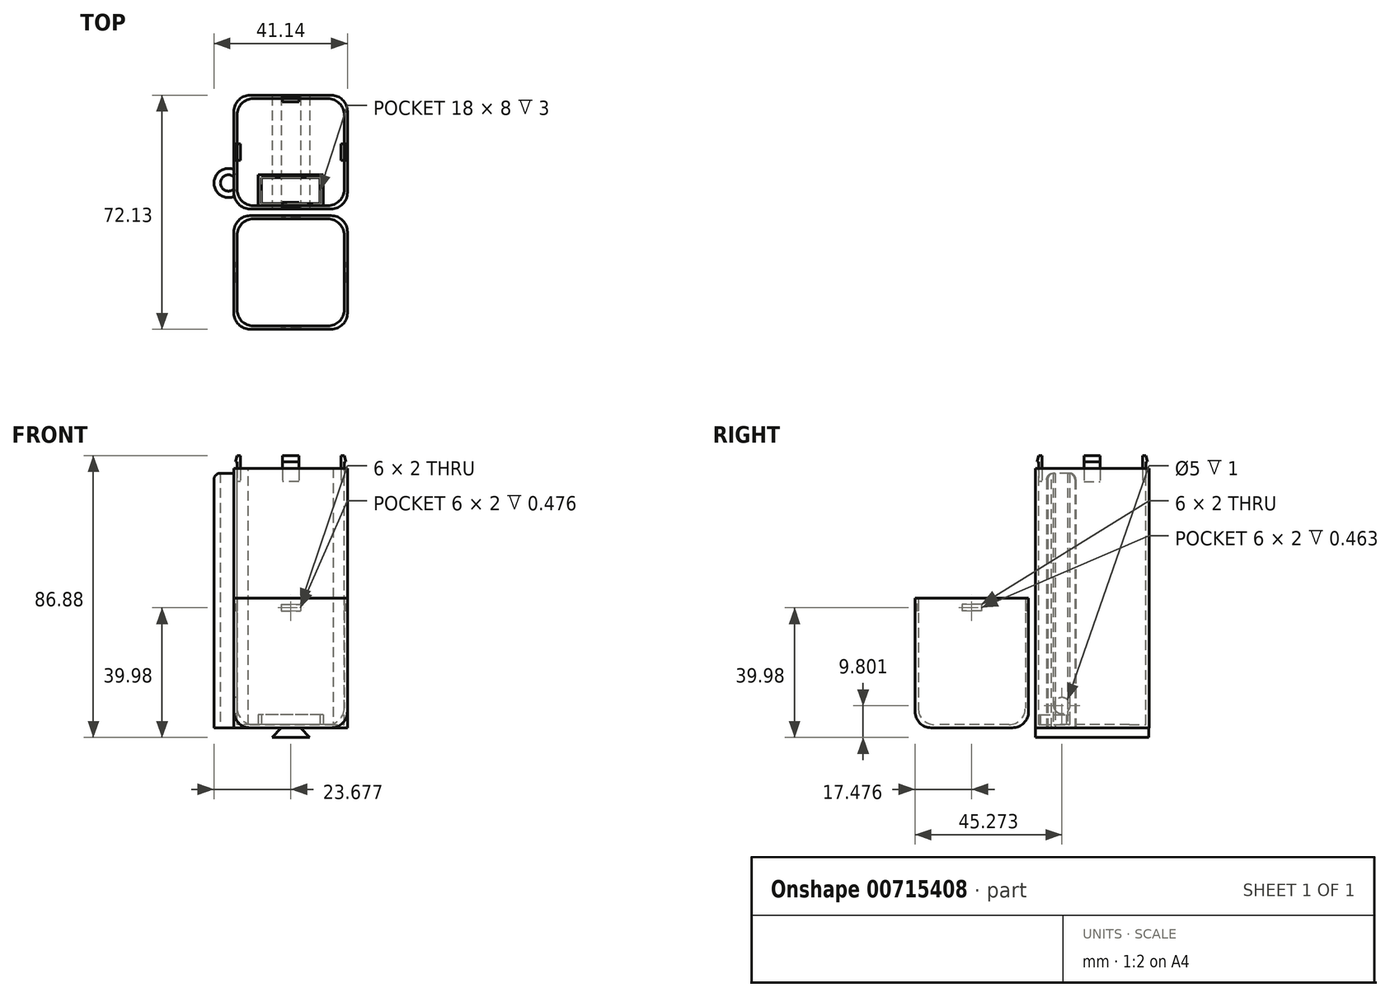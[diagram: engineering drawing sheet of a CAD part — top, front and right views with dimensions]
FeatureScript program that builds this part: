
annotation { "Feature Type Name" : "Feature", "Feature Type Description" : "" }
export const myFeature = defineFeature(function(context is Context, id is Id, definition is map)
    precondition{}
    {
        {
            var Q0;
            Q0=qCreatedBy(makeId("Top.planeOp"),FACE);
            var sketch = newSketch(context, id + "F0", { "sketchPlane" : qUnion([Q0])});
            skLineSegment(sketch, "E0.bottom", {"start": v(0, 0) * mm, "end": v(35, 0) * mm});
            skLineSegment(sketch, "E0.top", {"start": v(0, -35) * mm, "end": v(35, -35) * mm});
            skLineSegment(sketch, "E0.left", {"start": v(0, 0) * mm, "end": v(0, -35) * mm});
            skLineSegment(sketch, "E0.right", {"start": v(35, 0) * mm, "end": v(35, -35) * mm});
            skLineSegment(sketch, "E1.bottom", {"start": v(2.41, -2.74) * mm, "end": v(32.41, -2.74) * mm, "construction": true});
            skLineSegment(sketch, "E1.top", {"start": v(2.41, -32.74) * mm, "end": v(32.41, -32.74) * mm, "construction": true});
            skLineSegment(sketch, "E1.left", {"start": v(2.41, -2.74) * mm, "end": v(2.41, -32.74) * mm, "construction": true});
            skLineSegment(sketch, "E1.right", {"start": v(32.41, -2.74) * mm, "end": v(32.41, -32.74) * mm, "construction": true});
            skLineSegment(sketch, "E2.0", {"start": v(1, -1) * mm, "end": v(34, -1) * mm});
            skLineSegment(sketch, "E2.1", {"start": v(1, -1) * mm, "end": v(1, -34) * mm});
            skLineSegment(sketch, "E2.2", {"start": v(1, -34) * mm, "end": v(34, -34) * mm});
            skLineSegment(sketch, "E2.3", {"start": v(34, -1) * mm, "end": v(34, -34) * mm});
            skLineSegment(sketch, "E3", {"start": v(17.5, -35) * mm, "end": v(17.5, 0) * mm, "construction": true});
            skLineSegment(sketch, "E4", {"start": v(0, -17.5) * mm, "end": v(35, -17.5) * mm});
            skCircle(sketch, "E5", {"center": v(17.5, -17.5) * mm, "radius": 16.5 * mm});
            skSolve(sketch);
        }
        {
            var Q0;
            Q0 = qSketchRegion(id + "F0", true);
            extrude(context, id + "F1", {"entities" : qUnion([Q0]), "depth" : 40 * mm, "offsetDistance" : 25 * mm});
        }
        {
            var Q0;
            Q0 = qSketchRegion(id + "F0", true);
            extrude(context, id + "F2", {"entities" : qUnion([Q0]), "depth" : 80 * mm, "offsetDistance" : 25 * mm});
        }
        {
            var Q0;
            Q0=makeQuery(id+"F2.opExtrude","SWEPT_BODY",BODY,{"disambiguationData":[OSD([sQuery(id+"F0.wireOp",EDGE,"E0.bottom"),sQuery(id+"F0.wireOp",EDGE,"E0.top"),sQuery(id+"F0.wireOp",EDGE,"E0.left"),sQuery(id+"F0.wireOp",EDGE,"E0.right"),sQuery(id+"F0.wireOp",EDGE,"E2.0"),sQuery(id+"F0.wireOp",EDGE,"E2.1"),sQuery(id+"F0.wireOp",EDGE,"E2.2"),sQuery(id+"F0.wireOp",EDGE,"E2.3")])]});
            transform(context, id + "F3", {"entities" : qUnion([Q0]), "transformType" : TransformType.TRANSLATION_3D, "dx" : 0 * mm, "dy" : 0 * mm, "dz" : 45 * mm, "makeCopy" : false});
        }
        {
            var Q0;
            Q0=qCreatedBy(makeId("Top.planeOp"),FACE);
            var sketch = newSketch(context, id + "F4", { "sketchPlane" : qUnion([Q0])});
            skLineSegment(sketch, "E6.bottom", {"start": v(20.54, -0.52) * mm, "end": v(14.54, -0.52) * mm});
            skLineSegment(sketch, "E6.top", {"start": v(20.54, -34.52) * mm, "end": v(14.54, -34.52) * mm});
            skLineSegment(sketch, "E6.left", {"start": v(20.54, -0.52) * mm, "end": v(20.54, -34.52) * mm});
            skLineSegment(sketch, "E6.right", {"start": v(14.54, -0.52) * mm, "end": v(14.54, -34.52) * mm});
            skPoint(sketch, "E6.middle", {"position": v(17.54, -17.52) * mm});
            skPoint(sketch, "E6.middle.positionSnap0", {"position": v(14.24, -17.52) * mm});
            skLineSegment(sketch, "E7.bottom", {"start": v(34.54, -20.52) * mm, "end": v(0.54, -20.52) * mm});
            skLineSegment(sketch, "E7.top", {"start": v(34.54, -14.52) * mm, "end": v(0.54, -14.52) * mm});
            skLineSegment(sketch, "E7.left", {"start": v(34.54, -20.52) * mm, "end": v(34.54, -14.52) * mm});
            skLineSegment(sketch, "E7.right", {"start": v(0.54, -20.52) * mm, "end": v(0.54, -14.52) * mm});
            skSolve(sketch);
        }
        {
            var Q0;
            Q0 = qSketchRegion(id + "F4", true);
            extrude(context, id + "F5", {"entities" : qUnion([Q0]), "operationType" : NewBodyOperationType.REMOVE, "depth" : 38 * mm, "offsetDistance" : 25 * mm, "hasSecondDirection" : true, "secondDirectionOppositeDirection" : false, "secondDirectionDepth" : 36 * mm});
        }
        {
            var Q0;
            Q0=qCreatedBy(makeId("Right.planeOp"),FACE);
            var sketch = newSketch(context, id + "F6", { "sketchPlane" : qUnion([Q0])});
            skLineSegment(sketch, "E8.bottom", {"start": v(-33, 41.1) * mm, "end": v(-34, 41.1) * mm});
            skLineSegment(sketch, "E8.top", {"start": v(-33, 49.1) * mm, "end": v(-34, 49.1) * mm});
            skLineSegment(sketch, "E8.left", {"start": v(-33, 41.1) * mm, "end": v(-33, 49.1) * mm});
            skLineSegment(sketch, "E8.right", {"start": v(-34, 41.1) * mm, "end": v(-34, 49.1) * mm});
            skPoint(sketch, "E8.middle", {"position": v(-33.5, 45.1) * mm});
            skLineSegment(sketch, "E9", {"start": v(-34, 41.1) * mm, "end": v(-34.5, 43) * mm});
            skLineSegment(sketch, "E10", {"start": v(-34.5, 43) * mm, "end": v(-34, 43) * mm});
            skSolve(sketch);
        }
        {
            var Q0;
            {var subQ1=sQuery(id+"F6.wireOp",EDGE,"E8.bottom");Q0=makeQuery(id+"F6.imprint","IMPRINT",FACE,{"disambiguationData":[TD([[makeQuery(id+"F6.imprint","IMPRINT",EDGE,{"derivedFrom":subQ1}),-1.0]])]});}
            var Q1;
            {var subQ0=sQuery(id+"F6.wireOp",EDGE,"E9");Q1=makeQuery(id+"F6.imprint","IMPRINT",FACE,{"disambiguationData":[TD([[makeQuery(id+"F6.imprint","IMPRINT",EDGE,{"derivedFrom":subQ0}),-1.0]])]});}
            extrude(context, id + "F7", {"entities" : qUnion([Q0, Q1]), "depth" : 20 * mm, "offsetDistance" : 25 * mm, "hasSecondDirection" : true, "secondDirectionOppositeDirection" : false, "secondDirectionDepth" : 15 * mm});
        }
        {
            var Q0;
            Q0=makeQuery(id+"F7.opExtrude","SWEPT_BODY",BODY,{"disambiguationData":[OSD([sQuery(id+"F6.wireOp",EDGE,"E8.bottom"),sQuery(id+"F6.wireOp",EDGE,"E8.top"),sQuery(id+"F6.wireOp",EDGE,"E8.left"),sQuery(id+"F6.wireOp",EDGE,"E8.right"),sQuery(id+"F6.wireOp",EDGE,"E9"),sQuery(id+"F6.wireOp",EDGE,"E10")])]});
            var Q1;
            Q1=sQuery(id+"F0.wireOp",EDGE,"E5");
            circularPattern(context, id + "F8", {"operationType" : NewBodyOperationType.ADD, "entities" : qUnion([Q0]), "axis" : qUnion([Q1]), "angle" : 360 * degree, "instanceCount" : 4, "equalSpace" : true});
        }
        {
            var Q0;
            Q0=qCreatedBy(makeId("Top.planeOp"),FACE);
            var sketch = newSketch(context, id + "F9", { "sketchPlane" : qUnion([Q0])});
            skLineSegment(sketch, "E11.bottom", {"start": v(0, 37.13) * mm, "end": v(35, 37.13) * mm});
            skLineSegment(sketch, "E11.top", {"start": v(0, 2.13) * mm, "end": v(35, 2.13) * mm});
            skLineSegment(sketch, "E11.left", {"start": v(0, 37.13) * mm, "end": v(0, 2.13) * mm});
            skLineSegment(sketch, "E11.right", {"start": v(35, 37.13) * mm, "end": v(35, 2.13) * mm});
            skLineSegment(sketch, "E12", {"start": v(17.5, 37.13) * mm, "end": v(17.5, 2.13) * mm, "construction": true});
            skLineSegment(sketch, "E13", {"start": v(17.5, 2.13) * mm, "end": v(0, 19.63) * mm, "construction": true});
            skLineSegment(sketch, "E14", {"start": v(0, 19.63) * mm, "end": v(35, 19.63) * mm, "construction": true});
            skLineSegment(sketch, "E15", {"start": v(35, 19.63) * mm, "end": v(17.5, 37.13) * mm, "construction": true});
            skLineSegment(sketch, "E16.bottom", {"start": v(27.5, 2.67) * mm, "end": v(7.5, 2.67) * mm});
            skLineSegment(sketch, "E16.top", {"start": v(27.5, 12.67) * mm, "end": v(7.5, 12.67) * mm});
            skLineSegment(sketch, "E16.left", {"start": v(27.5, 2.67) * mm, "end": v(27.5, 12.67) * mm});
            skLineSegment(sketch, "E16.right", {"start": v(7.5, 2.67) * mm, "end": v(7.5, 12.67) * mm});
            skPoint(sketch, "E16.middle", {"position": v(17.5, 7.67) * mm});
            skLineSegment(sketch, "E17.0", {"start": v(26.5, 11.67) * mm, "end": v(8.5, 11.67) * mm});
            skLineSegment(sketch, "E17.1", {"start": v(26.5, 3.67) * mm, "end": v(26.5, 11.67) * mm});
            skLineSegment(sketch, "E17.2", {"start": v(26.5, 3.67) * mm, "end": v(8.5, 3.67) * mm});
            skLineSegment(sketch, "E17.3", {"start": v(8.5, 3.67) * mm, "end": v(8.5, 11.67) * mm});
            skSolve(sketch);
        }
        {
            var Q0;
            Q0=makeQuery(id+"F2.opExtrude","SWEPT_BODY",BODY,{"disambiguationData":[OSD([sQuery(id+"F0.wireOp",EDGE,"E0.bottom"),sQuery(id+"F0.wireOp",EDGE,"E0.top"),sQuery(id+"F0.wireOp",EDGE,"E0.left"),sQuery(id+"F0.wireOp",EDGE,"E0.right"),sQuery(id+"F0.wireOp",EDGE,"E2.0"),sQuery(id+"F0.wireOp",EDGE,"E2.1"),sQuery(id+"F0.wireOp",EDGE,"E2.2"),sQuery(id+"F0.wireOp",EDGE,"E2.3")])]});
            var Q1;
            Q1=makeQuery(id+"F8.opPattern","COPY",BODY,{"derivedFrom":makeQuery(id+"F7.opExtrude","SWEPT_BODY",BODY,{"disambiguationData":[OSD([sQuery(id+"F6.wireOp",EDGE,"E8.bottom"),sQuery(id+"F6.wireOp",EDGE,"E8.top"),sQuery(id+"F6.wireOp",EDGE,"E8.left"),sQuery(id+"F6.wireOp",EDGE,"E8.right"),sQuery(id+"F6.wireOp",EDGE,"E9"),sQuery(id+"F6.wireOp",EDGE,"E10")])]}),"instanceName":"1"});
            var Q2;
            Q2=makeQuery(id+"F8.opPattern","COPY",BODY,{"derivedFrom":makeQuery(id+"F7.opExtrude","SWEPT_BODY",BODY,{"disambiguationData":[OSD([sQuery(id+"F6.wireOp",EDGE,"E8.bottom"),sQuery(id+"F6.wireOp",EDGE,"E8.top"),sQuery(id+"F6.wireOp",EDGE,"E8.left"),sQuery(id+"F6.wireOp",EDGE,"E8.right"),sQuery(id+"F6.wireOp",EDGE,"E9"),sQuery(id+"F6.wireOp",EDGE,"E10")])]}),"instanceName":"3"});
            var Q3;
            Q3=makeQuery(id+"F7.opExtrude","SWEPT_BODY",BODY,{"disambiguationData":[OSD([sQuery(id+"F6.wireOp",EDGE,"E8.bottom"),sQuery(id+"F6.wireOp",EDGE,"E8.top"),sQuery(id+"F6.wireOp",EDGE,"E8.left"),sQuery(id+"F6.wireOp",EDGE,"E8.right"),sQuery(id+"F6.wireOp",EDGE,"E9"),sQuery(id+"F6.wireOp",EDGE,"E10")])]});
            var Q4;
            Q4=makeQuery(id+"F8.opPattern","COPY",BODY,{"derivedFrom":makeQuery(id+"F7.opExtrude","SWEPT_BODY",BODY,{"disambiguationData":[OSD([sQuery(id+"F6.wireOp",EDGE,"E8.bottom"),sQuery(id+"F6.wireOp",EDGE,"E8.top"),sQuery(id+"F6.wireOp",EDGE,"E8.left"),sQuery(id+"F6.wireOp",EDGE,"E8.right"),sQuery(id+"F6.wireOp",EDGE,"E9"),sQuery(id+"F6.wireOp",EDGE,"E10")])]}),"instanceName":"2"});
            var Q5;
            Q5=makeQuery(id+"F2.opExtrude","CAP_EDGE",EDGE,{"disambiguationData":[OSD([sQuery(id+"F0.wireOp",EDGE,"E0.bottom")])],"isStart":true});
            transform(context, id + "F10", {"entities" : qUnion([Q0, Q1, Q2, Q3, Q4]), "transformType" : TransformType.ROTATION, "transformAxis" : qUnion([Q5]), "angle" : 180 * degree, "makeCopy" : false});
        }
        {
            var Q0;
            Q0=makeQuery(id+"F2.opExtrude","SWEPT_BODY",BODY,{"disambiguationData":[OSD([sQuery(id+"F0.wireOp",EDGE,"E0.bottom"),sQuery(id+"F0.wireOp",EDGE,"E0.top"),sQuery(id+"F0.wireOp",EDGE,"E0.left"),sQuery(id+"F0.wireOp",EDGE,"E0.right"),sQuery(id+"F0.wireOp",EDGE,"E2.0"),sQuery(id+"F0.wireOp",EDGE,"E2.1"),sQuery(id+"F0.wireOp",EDGE,"E2.2"),sQuery(id+"F0.wireOp",EDGE,"E2.3")])]});
            var Q1;
            Q1=makeQuery(id+"F7.opExtrude","SWEPT_BODY",BODY,{"disambiguationData":[OSD([sQuery(id+"F6.wireOp",EDGE,"E8.bottom"),sQuery(id+"F6.wireOp",EDGE,"E8.top"),sQuery(id+"F6.wireOp",EDGE,"E8.left"),sQuery(id+"F6.wireOp",EDGE,"E8.right"),sQuery(id+"F6.wireOp",EDGE,"E9"),sQuery(id+"F6.wireOp",EDGE,"E10")])]});
            var Q2;
            Q2=makeQuery(id+"F8.opPattern","COPY",BODY,{"derivedFrom":makeQuery(id+"F7.opExtrude","SWEPT_BODY",BODY,{"disambiguationData":[OSD([sQuery(id+"F6.wireOp",EDGE,"E8.bottom"),sQuery(id+"F6.wireOp",EDGE,"E8.top"),sQuery(id+"F6.wireOp",EDGE,"E8.left"),sQuery(id+"F6.wireOp",EDGE,"E8.right"),sQuery(id+"F6.wireOp",EDGE,"E9"),sQuery(id+"F6.wireOp",EDGE,"E10")])]}),"instanceName":"1"});
            var Q3;
            Q3=makeQuery(id+"F8.opPattern","COPY",BODY,{"derivedFrom":makeQuery(id+"F7.opExtrude","SWEPT_BODY",BODY,{"disambiguationData":[OSD([sQuery(id+"F6.wireOp",EDGE,"E8.bottom"),sQuery(id+"F6.wireOp",EDGE,"E8.top"),sQuery(id+"F6.wireOp",EDGE,"E8.left"),sQuery(id+"F6.wireOp",EDGE,"E8.right"),sQuery(id+"F6.wireOp",EDGE,"E9"),sQuery(id+"F6.wireOp",EDGE,"E10")])]}),"instanceName":"2"});
            var Q4;
            Q4=makeQuery(id+"F8.opPattern","COPY",BODY,{"derivedFrom":makeQuery(id+"F7.opExtrude","SWEPT_BODY",BODY,{"disambiguationData":[OSD([sQuery(id+"F6.wireOp",EDGE,"E8.bottom"),sQuery(id+"F6.wireOp",EDGE,"E8.top"),sQuery(id+"F6.wireOp",EDGE,"E8.left"),sQuery(id+"F6.wireOp",EDGE,"E8.right"),sQuery(id+"F6.wireOp",EDGE,"E9"),sQuery(id+"F6.wireOp",EDGE,"E10")])]}),"instanceName":"3"});
            transform(context, id + "F11", {"entities" : qUnion([Q0, Q1, Q2, Q3, Q4]), "transformType" : TransformType.TRANSLATION_3D, "dx" : 0 * mm, "dy" : 2.1 * mm, "dz" : 35 * mm, "makeCopy" : false});
        }
        {
            var Q0;
            {var subQ7=sQuery(id+"F0.wireOp",EDGE,"E0.top");Q0=makeQuery(id+"F0.imprint","IMPRINT",FACE,{"disambiguationData":[TD([[makeQuery(id+"F0.imprint","IMPRINT",EDGE,{"derivedFrom":subQ7}),1.0]])]});}
            var Q1;
            {var subQ6=sQuery(id+"F0.wireOp",EDGE,"E0.bottom");Q1=makeQuery(id+"F0.imprint","IMPRINT",FACE,{"disambiguationData":[TD([[makeQuery(id+"F0.imprint","IMPRINT",EDGE,{"derivedFrom":subQ6}),-1.0]])]});}
            var Q2;
            {var subQ0=sQuery(id+"F0.wireOp",EDGE,"E2.1");var subQ1=sQuery(id+"F0.wireOp",EDGE,"E2.0");var subQ2=makeQuery(id+"F0.imprint","INTERSECT",VERTEX,{"derivedFrom":[subQ1,subQ0]});Q2=makeQuery(id+"F0.imprint","IMPRINT",FACE,{"disambiguationData":[TD([[makeQuery(id+"F0.imprint","IMPRINT",EDGE,{"disambiguationData":[TD([[subQ2,-1.0]])],"derivedFrom":subQ1}),-1.0]])]});}
            var Q3;
            {var subQ0=sQuery(id+"F0.wireOp",EDGE,"E5");var subQ4=makeQuery(id+"F0.imprint","INTERSECT",VERTEX,{"derivedFrom":[sQuery(id+"F0.wireOp",EDGE,"E2.2"),subQ0]});Q3=makeQuery(id+"F0.imprint","IMPRINT",FACE,{"disambiguationData":[TD([[makeQuery(id+"F0.imprint","IMPRINT",EDGE,{"disambiguationData":[TD([[subQ4,1.0]])],"derivedFrom":subQ0}),1.0]])]});}
            var Q4;
            {var subQ0=sQuery(id+"F0.wireOp",EDGE,"E2.2");var subQ1=sQuery(id+"F0.wireOp",EDGE,"E2.1");var subQ2=makeQuery(id+"F0.imprint","INTERSECT",VERTEX,{"derivedFrom":[subQ1,subQ0]});Q4=makeQuery(id+"F0.imprint","IMPRINT",FACE,{"disambiguationData":[TD([[makeQuery(id+"F0.imprint","IMPRINT",EDGE,{"disambiguationData":[TD([[subQ2,-1.0]])],"derivedFrom":subQ0}),1.0]])]});}
            var Q5;
            {var subQ0=sQuery(id+"F0.wireOp",EDGE,"E2.3");var subQ1=sQuery(id+"F0.wireOp",EDGE,"E2.2");var subQ2=makeQuery(id+"F0.imprint","INTERSECT",VERTEX,{"derivedFrom":[subQ1,subQ0]});Q5=makeQuery(id+"F0.imprint","IMPRINT",FACE,{"disambiguationData":[TD([[makeQuery(id+"F0.imprint","IMPRINT",EDGE,{"disambiguationData":[TD([[subQ2,1.0]])],"derivedFrom":subQ1}),1.0]])]});}
            var Q6;
            {var subQ0=sQuery(id+"F0.wireOp",EDGE,"E5");var subQ4=makeQuery(id+"F0.imprint","INTERSECT",VERTEX,{"derivedFrom":[sQuery(id+"F0.wireOp",EDGE,"E2.0"),subQ0]});Q6=makeQuery(id+"F0.imprint","IMPRINT",FACE,{"disambiguationData":[TD([[makeQuery(id+"F0.imprint","IMPRINT",EDGE,{"disambiguationData":[TD([[subQ4,1.0]])],"derivedFrom":subQ0}),1.0]])]});}
            var Q7;
            {var subQ0=sQuery(id+"F0.wireOp",EDGE,"E2.3");var subQ1=sQuery(id+"F0.wireOp",EDGE,"E2.0");var subQ2=makeQuery(id+"F0.imprint","INTERSECT",VERTEX,{"derivedFrom":[subQ1,subQ0]});Q7=makeQuery(id+"F0.imprint","IMPRINT",FACE,{"disambiguationData":[TD([[makeQuery(id+"F0.imprint","IMPRINT",EDGE,{"disambiguationData":[TD([[subQ2,1.0]])],"derivedFrom":subQ1}),-1.0]])]});}
            var Q8;
            Q8=sQuery(id+"F0.wireOp",EDGE,"E0.right");
            var Q9;
            Q9=sQuery(id+"F0.wireOp",EDGE,"E0.top");
            var Q10;
            Q10=sQuery(id+"F0.wireOp",EDGE,"E0.left");
            var Q11;
            Q11=sQuery(id+"F0.wireOp",EDGE,"E0.bottom");
            extrude(context, id + "F12", {"entities" : qUnion([Q0, Q1, Q2, Q3, Q4, Q5, Q6, Q7]), "operationType" : NewBodyOperationType.ADD, "surfaceEntities" : qUnion([Q8, Q9, Q10, Q11]), "depth" : 1 * mm, "offsetDistance" : 25 * mm});
        }
        {
            var Q0;
            Q0=makeQuery(id+"F9.imprint","IMPRINT",FACE,{"disambiguationData":[TD([[makeQuery(id+"F9.imprint","IMPRINT",EDGE,{"derivedFrom":sQuery(id+"F9.wireOp",EDGE,"E16.bottom")}),-1.0]])]});
            extrude(context, id + "F13", {"entities" : qUnion([Q0]), "operationType" : NewBodyOperationType.ADD, "depth" : 4 * mm, "offsetDistance" : 25 * mm, "hasSecondDirection" : true, "secondDirectionOppositeDirection" : true, "secondDirectionDepth" : -1 * mm});
        }
        {
            var Q0;
            Q0 = qSketchRegion(id + "F9", true);
            var Q1;
            Q1=makeQuery(id+"F9.imprint","IMPRINT",FACE,{"disambiguationData":[TD([[makeQuery(id+"F9.imprint","IMPRINT",EDGE,{"derivedFrom":sQuery(id+"F9.wireOp",EDGE,"E17.0")}),1.0]])]});
            var Q2;
            Q2=makeQuery(id+"F9.imprint","IMPRINT",FACE,{"disambiguationData":[TD([[makeQuery(id+"F9.imprint","IMPRINT",EDGE,{"derivedFrom":sQuery(id+"F9.wireOp",EDGE,"E16.bottom")}),-1.0]])]});
            extrude(context, id + "F14", {"entities" : qUnion([Q0, Q1, Q2]), "operationType" : NewBodyOperationType.ADD, "depth" : 1 * mm, "offsetDistance" : 25 * mm});
        }
        {
            var Q0;
            Q0=makeQuery(id+"F1.opExtrude","SWEPT_EDGE",EDGE,{"disambiguationData":[OSD([sQuery(id+"F0.wireOp",EDGE,"E0.top"),sQuery(id+"F0.wireOp",EDGE,"E0.left")])]});
            var Q1;
            Q1=makeQuery(id+"F1.opExtrude","SWEPT_EDGE",EDGE,{"disambiguationData":[OSD([sQuery(id+"F0.wireOp",EDGE,"E2.1"),sQuery(id+"F0.wireOp",EDGE,"E2.2")])]});
            var Q2;
            Q2=makeQuery(id+"F1.opExtrude","SWEPT_EDGE",EDGE,{"disambiguationData":[OSD([sQuery(id+"F0.wireOp",EDGE,"E2.2"),sQuery(id+"F0.wireOp",EDGE,"E2.3")])]});
            var Q3;
            Q3=makeQuery(id+"F1.opExtrude","SWEPT_EDGE",EDGE,{"disambiguationData":[OSD([sQuery(id+"F0.wireOp",EDGE,"E2.0"),sQuery(id+"F0.wireOp",EDGE,"E2.3")])]});
            var Q4;
            Q4=makeQuery(id+"F1.opExtrude","SWEPT_EDGE",EDGE,{"disambiguationData":[OSD([sQuery(id+"F0.wireOp",EDGE,"E2.0"),sQuery(id+"F0.wireOp",EDGE,"E2.1")])]});
            var Q5;
            Q5=makeQuery(id+"F1.opExtrude","SWEPT_EDGE",EDGE,{"disambiguationData":[OSD([sQuery(id+"F0.wireOp",EDGE,"E0.top"),sQuery(id+"F0.wireOp",EDGE,"E0.right")])]});
            var Q6;
            Q6=makeQuery(id+"F1.opExtrude","SWEPT_EDGE",EDGE,{"disambiguationData":[OSD([sQuery(id+"F0.wireOp",EDGE,"E0.bottom"),sQuery(id+"F0.wireOp",EDGE,"E0.right")])]});
            var Q7;
            Q7=makeQuery(id+"F1.opExtrude","SWEPT_EDGE",EDGE,{"disambiguationData":[OSD([sQuery(id+"F0.wireOp",EDGE,"E0.bottom"),sQuery(id+"F0.wireOp",EDGE,"E0.left")])]});
            fillet(context, id + "F15", {"entities" : qUnion([Q0, Q1, Q2, Q3, Q4, Q5, Q6, Q7]), "radius" : 5 * mm, "allowEdgeOverflow" : false});
        }
        {
            var Q0;
            Q0=makeQuery(id+"F14.opExtrude","SWEPT_EDGE",EDGE,{"disambiguationData":[OSD([sQuery(id+"F9.wireOp",EDGE,"E11.bottom"),sQuery(id+"F9.wireOp",EDGE,"E11.left")])]});
            var Q1;
            Q1=makeQuery(id+"F14.opExtrude","SWEPT_EDGE",EDGE,{"disambiguationData":[OSD([sQuery(id+"F9.wireOp",EDGE,"E11.bottom"),sQuery(id+"F9.wireOp",EDGE,"E11.right")])]});
            var Q2;
            Q2=makeQuery(id+"F2.opExtrude","SWEPT_EDGE",EDGE,{"disambiguationData":[OSD([sQuery(id+"F0.wireOp",EDGE,"E0.bottom"),sQuery(id+"F0.wireOp",EDGE,"E0.right")])]});
            var Q3;
            Q3=makeQuery(id+"F2.opExtrude","SWEPT_EDGE",EDGE,{"disambiguationData":[OSD([sQuery(id+"F0.wireOp",EDGE,"E0.bottom"),sQuery(id+"F0.wireOp",EDGE,"E0.left")])]});
            var Q4;
            Q4=makeQuery(id+"F2.opExtrude","SWEPT_EDGE",EDGE,{"disambiguationData":[OSD([sQuery(id+"F0.wireOp",EDGE,"E2.1"),sQuery(id+"F0.wireOp",EDGE,"E2.2")])]});
            var Q5;
            Q5=makeQuery(id+"F2.opExtrude","SWEPT_EDGE",EDGE,{"disambiguationData":[OSD([sQuery(id+"F0.wireOp",EDGE,"E2.0"),sQuery(id+"F0.wireOp",EDGE,"E2.1")])]});
            var Q6;
            Q6=makeQuery(id+"F2.opExtrude","SWEPT_EDGE",EDGE,{"disambiguationData":[OSD([sQuery(id+"F0.wireOp",EDGE,"E2.2"),sQuery(id+"F0.wireOp",EDGE,"E2.3")])]});
            var Q7;
            Q7=makeQuery(id+"F2.opExtrude","SWEPT_EDGE",EDGE,{"disambiguationData":[OSD([sQuery(id+"F0.wireOp",EDGE,"E2.0"),sQuery(id+"F0.wireOp",EDGE,"E2.3")])]});
            fillet(context, id + "F16", {"entities" : qUnion([Q0, Q1, Q2, Q3, Q4, Q5, Q6, Q7]), "radius" : 5 * mm, "tangentPropagation" : true, "allowEdgeOverflow" : false});
        }
        {
            var Q0;
            Q0=makeQuery(id+"F1.opExtrude","CAP_EDGE",EDGE,{"disambiguationData":[OSD([sQuery(id+"F0.wireOp",EDGE,"E0.top")])],"isStart":true});
            var Q1;
            Q1=makeQuery(id+"F1.opExtrude","CAP_EDGE",EDGE,{"disambiguationData":[OSD([sQuery(id+"F0.wireOp",EDGE,"E0.right")])],"isStart":true});
            var Q2;
            Q2=makeQuery(id+"F1.opExtrude","CAP_EDGE",EDGE,{"disambiguationData":[OSD([sQuery(id+"F0.wireOp",EDGE,"E0.bottom")])],"isStart":true});
            var Q3;
            Q3=makeQuery(id+"F1.opExtrude","CAP_EDGE",EDGE,{"disambiguationData":[OSD([sQuery(id+"F0.wireOp",EDGE,"E0.left")])],"isStart":true});
            var Q4;
            Q4=makeQuery(id+"F12.boolean.opBoolean","INTERSECT",EDGE,{"derivedFrom":[makeQuery(id+"F1.opExtrude","SWEPT_FACE",FACE,{"disambiguationData":[OSD([sQuery(id+"F0.wireOp",EDGE,"E2.1")])]}),makeQuery(id+"F12.opExtrude","CAP_FACE",FACE,{"disambiguationData":[OSD([sQuery(id+"F0.wireOp",EDGE,"E0.bottom"),sQuery(id+"F0.wireOp",EDGE,"E0.top"),sQuery(id+"F0.wireOp",EDGE,"E0.left"),sQuery(id+"F0.wireOp",EDGE,"E0.right")])],"isStart":false})]});
            var Q5;
            Q5=makeQuery(id+"F12.boolean.opBoolean","INTERSECT",EDGE,{"derivedFrom":[makeQuery(id+"F1.opExtrude","SWEPT_FACE",FACE,{"disambiguationData":[OSD([sQuery(id+"F0.wireOp",EDGE,"E2.0")])]}),makeQuery(id+"F12.opExtrude","CAP_FACE",FACE,{"disambiguationData":[OSD([sQuery(id+"F0.wireOp",EDGE,"E0.bottom"),sQuery(id+"F0.wireOp",EDGE,"E0.top"),sQuery(id+"F0.wireOp",EDGE,"E0.left"),sQuery(id+"F0.wireOp",EDGE,"E0.right")])],"isStart":false})]});
            var Q6;
            Q6=makeQuery(id+"F12.boolean.opBoolean","INTERSECT",EDGE,{"derivedFrom":[makeQuery(id+"F1.opExtrude","SWEPT_FACE",FACE,{"disambiguationData":[OSD([sQuery(id+"F0.wireOp",EDGE,"E2.3")])]}),makeQuery(id+"F12.opExtrude","CAP_FACE",FACE,{"disambiguationData":[OSD([sQuery(id+"F0.wireOp",EDGE,"E0.bottom"),sQuery(id+"F0.wireOp",EDGE,"E0.top"),sQuery(id+"F0.wireOp",EDGE,"E0.left"),sQuery(id+"F0.wireOp",EDGE,"E0.right")])],"isStart":false})]});
            var Q7;
            Q7=makeQuery(id+"F12.boolean.opBoolean","INTERSECT",EDGE,{"derivedFrom":[makeQuery(id+"F1.opExtrude","SWEPT_FACE",FACE,{"disambiguationData":[OSD([sQuery(id+"F0.wireOp",EDGE,"E2.2")])]}),makeQuery(id+"F12.opExtrude","CAP_FACE",FACE,{"disambiguationData":[OSD([sQuery(id+"F0.wireOp",EDGE,"E0.bottom"),sQuery(id+"F0.wireOp",EDGE,"E0.top"),sQuery(id+"F0.wireOp",EDGE,"E0.left"),sQuery(id+"F0.wireOp",EDGE,"E0.right")])],"isStart":false})]});
            fillet(context, id + "F17", {"entities" : qUnion([Q0, Q1, Q2, Q3, Q4, Q5, Q6, Q7]), "radius" : 5 * mm, "tangentPropagation" : true, "allowEdgeOverflow" : false});
        }
        {
            var Q0;
            Q0=makeQuery(id+"F14.boolean.opBoolean","MERGE",FACE,{"derivedFrom":[makeQuery(id+"F2.opExtrude","SWEPT_FACE",FACE,{"disambiguationData":[OSD([sQuery(id+"F0.wireOp",EDGE,"E0.left")])]}),makeQuery(id+"F14.opExtrude","SWEPT_FACE",FACE,{"disambiguationData":[OSD([sQuery(id+"F9.wireOp",EDGE,"E11.left")])]})]});
            var sketch = newSketch(context, id + "F18", { "sketchPlane" : qUnion([Q0])});
            skCircle(sketch, "E18", {"center": v(-10.27, 6.82) * mm, "radius": 2.5 * mm});
            skSolve(sketch);
        }
        {
            var Q0;
            Q0=makeQuery(id+"F18.imprint","IMPRINT",FACE,{"disambiguationData":[TD([[makeQuery(id+"F18.imprint","IMPRINT",EDGE,{"derivedFrom":sQuery(id+"F18.wireOp",EDGE,"E18")}),1.0]])]});
            extrude(context, id + "F19", {"entities" : qUnion([Q0]), "operationType" : NewBodyOperationType.REMOVE, "oppositeDirection" : true, "depth" : 25 * mm, "offsetDistance" : 25 * mm});
        }
        {
            var Q0;
            Q0=qCreatedBy(makeId("Top.planeOp"),FACE);
            var sketch = newSketch(context, id + "F20", { "sketchPlane" : qUnion([Q0])});
            skCircle(sketch, "E19", {"center": v(-1.64, 10.08) * mm, "radius": 2.5 * mm});
            skCircle(sketch, "E20.0", {"center": v(-1.64, 10.08) * mm, "radius": 4.5 * mm});
            skLineSegment(sketch, "E21", {"start": v(0, 5.9) * mm, "end": v(0, 14.27) * mm});
            skSolve(sketch);
        }
        {
            var Q0;
            {var subQ0=sQuery(id+"F20.wireOp",EDGE,"E21");var subQ1=sQuery(id+"F20.wireOp",EDGE,"E19");var subQ2=makeQuery(id+"F20.imprint","INTERSECT",VERTEX,{"disambiguationData":[OD(0.0)],"derivedFrom":[subQ1,subQ0]});Q0=makeQuery(id+"F20.imprint","IMPRINT",FACE,{"disambiguationData":[TD([[makeQuery(id+"F20.imprint","IMPRINT",EDGE,{"disambiguationData":[TD([[subQ2,1.0]])],"derivedFrom":subQ1}),-1.0]])]});}
            extrude(context, id + "F21", {"entities" : qUnion([Q0]), "operationType" : NewBodyOperationType.ADD, "depth" : 78.5 * mm, "offsetDistance" : 25 * mm});
        }
        {
            var Q0;
            Q0=qCreatedBy(makeId("Front.planeOp"),FACE);
            var sketch = newSketch(context, id + "F22", { "sketchPlane" : qUnion([Q0])});
            skLineSegment(sketch, "E22.bottom", {"start": v(11.84, 0.2) * mm, "end": v(23.31, 0.2) * mm});
            skLineSegment(sketch, "E22.top", {"start": v(11.84, -2.98) * mm, "end": v(23.31, -2.98) * mm});
            skLineSegment(sketch, "E22.left", {"start": v(11.84, 0.2) * mm, "end": v(11.84, -2.98) * mm});
            skLineSegment(sketch, "E22.right", {"start": v(23.31, 0.2) * mm, "end": v(23.31, -2.98) * mm});
            skPoint(sketch, "E22.middle", {"position": v(17.57, -1.39) * mm});
            skLineSegment(sketch, "E23", {"start": v(23.31, -2.98) * mm, "end": v(20.43, 0.21) * mm});
            skLineSegment(sketch, "E24", {"start": v(11.84, -2.98) * mm, "end": v(14.72, 0.21) * mm});
            skLineSegment(sketch, "E25", {"start": v(10.1, -3) * mm, "end": v(26.32, -3) * mm, "construction": true});
            skSolve(sketch);
        }
        {
            var Q0;
            Q0=makeQuery(id+"F22.imprint","IMPRINT",FACE,{"disambiguationData":[TD([[makeQuery(id+"F22.imprint","IMPRINT",EDGE,{"derivedFrom":sQuery(id+"F22.wireOp",EDGE,"E22.top")}),1.0]])]});
            extrude(context, id + "F23", {"entities" : qUnion([Q0]), "operationType" : NewBodyOperationType.ADD, "oppositeDirection" : true, "depth" : 37 * mm, "offsetDistance" : 25 * mm, "hasSecondDirection" : true, "secondDirectionOppositeDirection" : true, "secondDirectionDepth" : 2.1 * mm});
        }
        {
            var Q0;
            Q0=makeQuery(id+"F21.opExtrude","CAP_EDGE",EDGE,{"disambiguationData":[OSD([sQuery(id+"F20.wireOp",EDGE,"E20.0")])],"isStart":false});
            fillet(context, id + "F24", {"entities" : qUnion([Q0]), "radius" : 2 * mm, "tangentPropagation" : true, "allowEdgeOverflow" : false});
        }
    });
